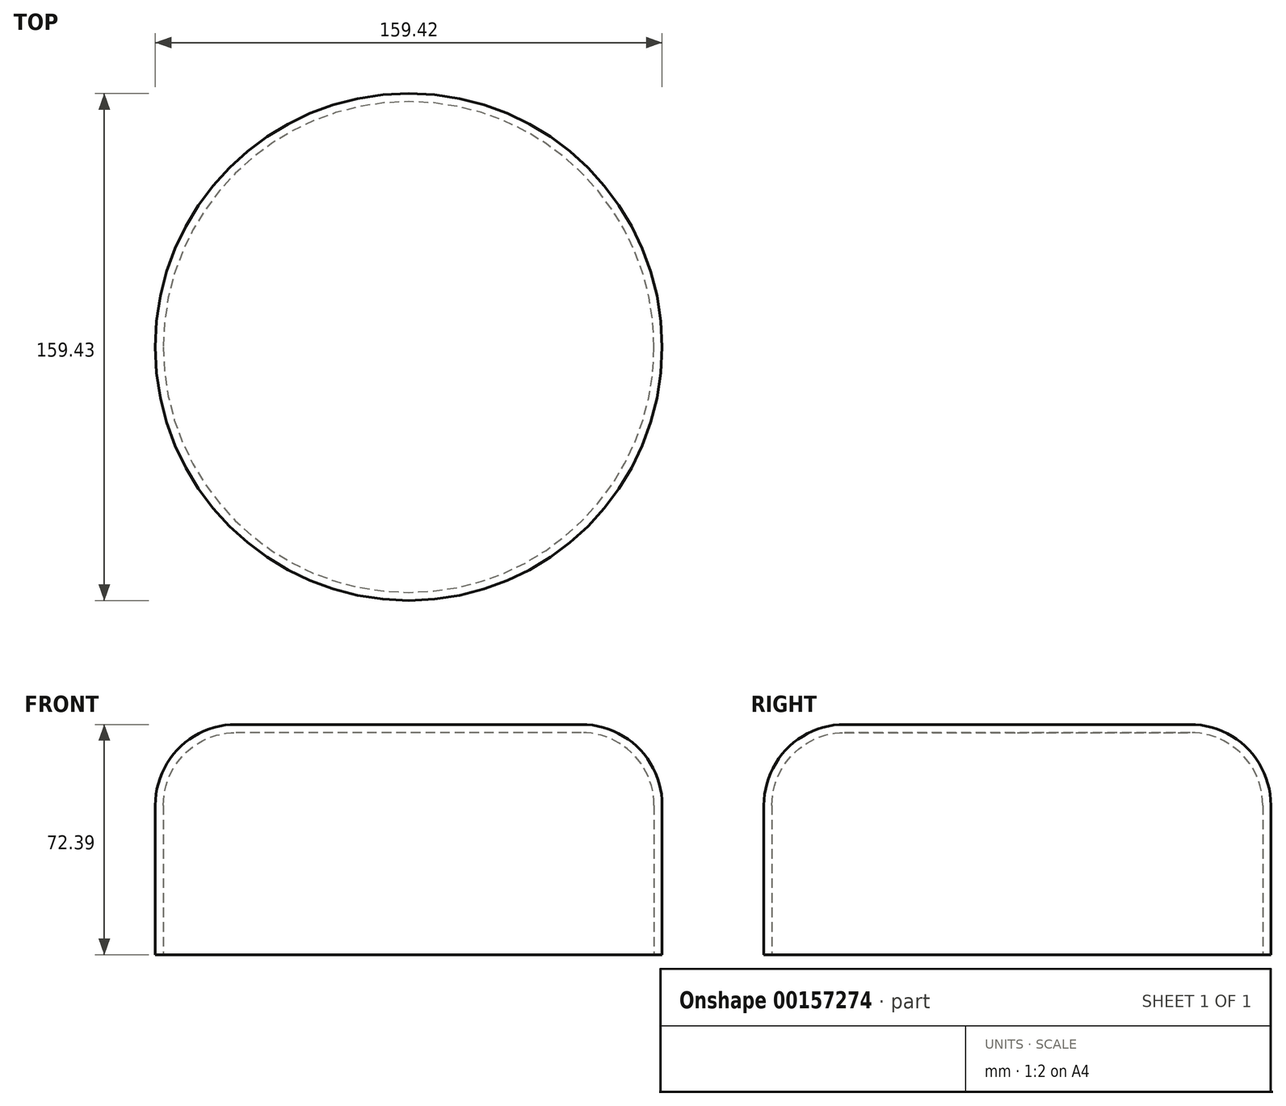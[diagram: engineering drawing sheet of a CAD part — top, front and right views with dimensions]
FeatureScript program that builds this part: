
annotation { "Feature Type Name" : "Feature", "Feature Type Description" : "" }
export const myFeature = defineFeature(function(context is Context, id is Id, definition is map)
    precondition{}
    {
        {
            var Q0;
            Q0=qCreatedBy(makeId("Top.planeOp"),FACE);
            var sketch = newSketch(context, id + "F0", { "sketchPlane" : qUnion([Q0])});
            skCircle(sketch, "E0", {"center": v(-31.04, 11.33) * mm, "radius": 79.71 * mm});
            skSolve(sketch);
        }
        {
            var Q0;
            Q0 = qSketchRegion(id + "F0", true);
            extrude(context, id + "F1", {"entities" : qUnion([Q0]), "depth" : 72.39 * mm, "offsetDistance" : 25.4 * mm});
        }
        {
            var Q0;
            Q0=makeQuery(id+"F1.opExtrude","CAP_EDGE",EDGE,{"disambiguationData":[OSD([sQuery(id+"F0.wireOp",EDGE,"E0")])],"isStart":false});
            fillet(context, id + "F2", {"entities" : qUnion([Q0]), "tangentPropagation" : true, "radius" : 25.4 * mm, "defaultsChanged" : true, "vertexSettings" : [], "allowEdgeOverflow" : false});
        }
        {
            var Q0;
            Q0=makeQuery(id+"F1.opExtrude","CAP_FACE",FACE,{"disambiguationData":[OSD([sQuery(id+"F0.wireOp",EDGE,"E0")])],"isStart":true});
            shell(context, id + "F3", {"entities" : qUnion([Q0]), "thickness" : 2.54 * mm});
        }
    });
